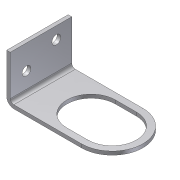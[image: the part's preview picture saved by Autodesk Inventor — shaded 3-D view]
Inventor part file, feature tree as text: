
AUTODESK INVENTOR PART (.ipt)
format: ipt  version: 2014 SP1 (Build 180222100, 222)  size: 122,368 bytes
history: native  units: mm (DEFAULTED — no unit token found)
features: sheet_metal_op x3, sketch x3, other x3, projected_geometry x1
ambient origin geometry x8: Origin, YZ Plane, XZ Plane, XY Plane, X Axis, Y Axis, Z Axis, Center Point
bodies: Solid1 (feature_tree)
feature tree (10):
  sheet_metal_op  "Face1"
  sheet_metal_op  "Flange1"
  sketch  "Sketch1"  dims[d0=38.0mm]
  other  "Plate1"
  sketch  "Sketch2"  dims[d1=63.0mm]
  other  "Plate2"
  sheet_metal_op  "Bend1"
  sketch  "Sketch3"  dims[d2=4.0mm d3=43.0mm d4=2.2mm d5=2.2mm d6=1.1mm d7=4.4mm d8=2.2mm d9=27.0mm d10=90.0deg d11=2.2mm d12=5.5mm d13=9.5mm d14=7.5mm d15=10.0mm d16=15.0mm d17=2.2mm d18=0.0mm]
  projected_geometry  "Projected Loop1"
  other  "Cut1"
